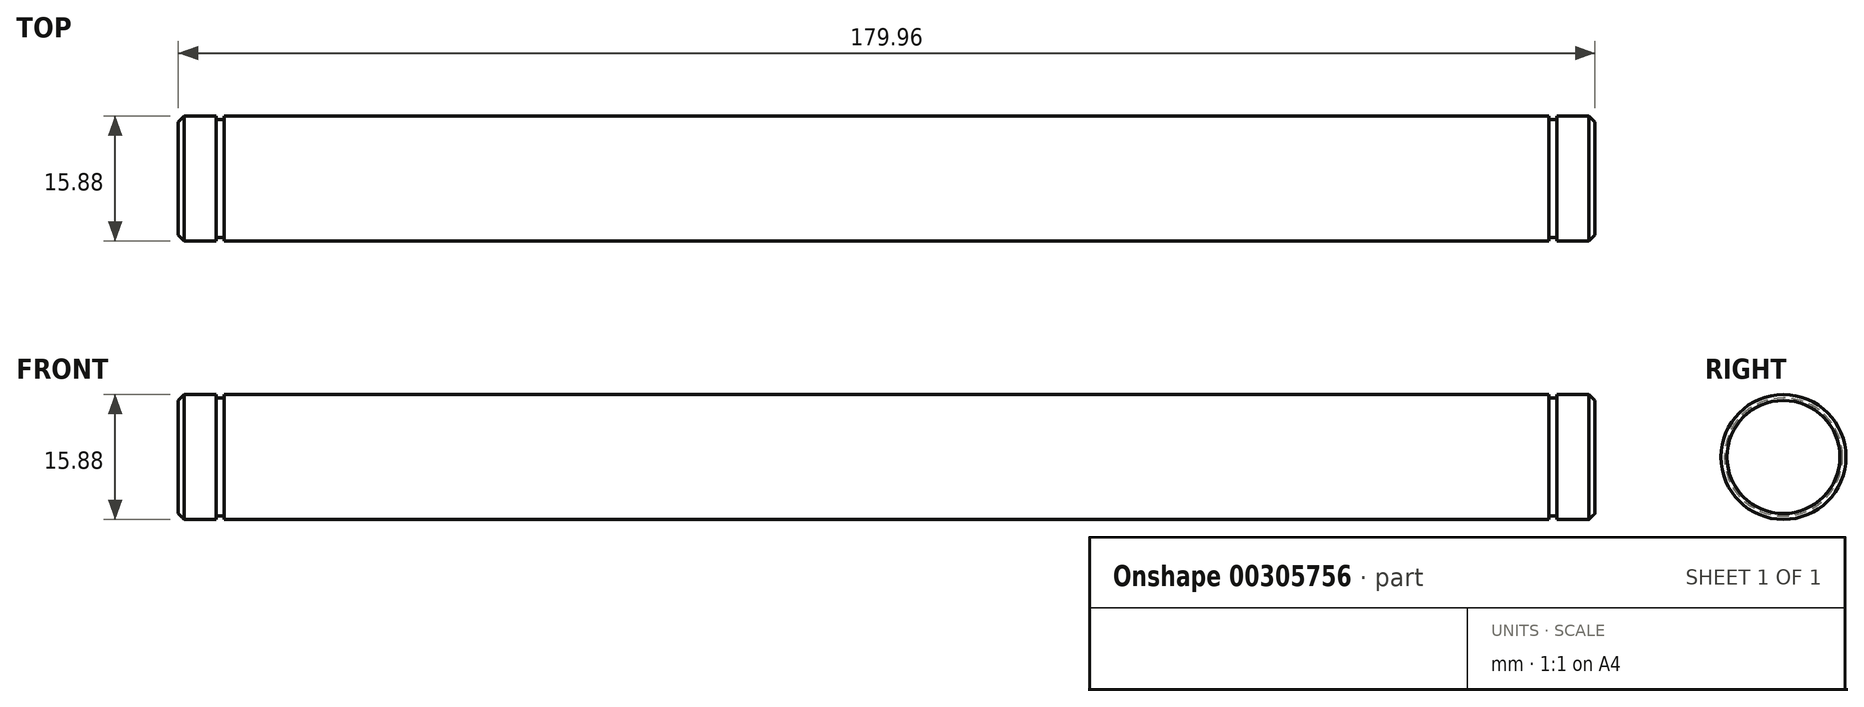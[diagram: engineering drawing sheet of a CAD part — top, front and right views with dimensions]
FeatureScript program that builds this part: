
annotation { "Feature Type Name" : "Feature", "Feature Type Description" : "" }
export const myFeature = defineFeature(function(context is Context, id is Id, definition is map)
    precondition{}
    {
        {
            var Q0;
            Q0=qCreatedBy(makeId("Right.planeOp"),FACE);
            var sketch = newSketch(context, id + "F0", { "sketchPlane" : qUnion([Q0])});
            skCircle(sketch, "E0", {"center": v(0, 0) * mm, "radius": 7.94 * mm});
            skSolve(sketch);
        }
        {
            var Q0;
            Q0 = qSketchRegion(id + "F0", true);
            extrude(context, id + "F1", {"entities" : qUnion([Q0]), "endBound" : BoundingType.SYMMETRIC, "depth" : 168.27 * mm});
        }
        {
            var Q0;
            Q0=makeQuery(id+"F1.opExtrude","CAP_FACE",FACE,{"disambiguationData":[OSD([sQuery(id+"F0.wireOp",EDGE,"E0")])],"isStart":false});
            var sketch = newSketch(context, id + "F2", { "sketchPlane" : qUnion([Q0])});
            skCircle(sketch, "E1", {"center": v(0, 0) * mm, "radius": 7.5 * mm});
            skSolve(sketch);
        }
        {
            var Q0;
            Q0 = qSketchRegion(id + "F2", true);
            extrude(context, id + "F3", {"entities" : qUnion([Q0]), "depth" : 1.02 * mm});
        }
        {
            var Q0;
            Q0=makeQuery(id+"F3.opExtrude","CAP_FACE",FACE,{"disambiguationData":[OSD([sQuery(id+"F2.wireOp",EDGE,"E1")])],"isStart":false});
            var sketch = newSketch(context, id + "F4", { "sketchPlane" : qUnion([Q0])});
            skCircle(sketch, "E2", {"center": v(0, 0) * mm, "radius": 7.94 * mm});
            skSolve(sketch);
        }
        {
            var Q0;
            Q0 = qSketchRegion(id + "F4", true);
            extrude(context, id + "F5", {"entities" : qUnion([Q0]), "operationType" : NewBodyOperationType.ADD, "depth" : 4.83 * mm});
        }
        {
            var Q0;
            Q0=makeQuery(id+"F5.opExtrude","CAP_FACE",FACE,{"disambiguationData":[OSD([sQuery(id+"F4.wireOp",EDGE,"E2")])],"isStart":false});
            chamfer(context, id + "F6", {"entities" : qUnion([Q0]), "width" : 0.76 * mm, "tangentPropagation" : true});
        }
        {
            var Q0;
            Q0=makeQuery(id+"F3.opExtrude","SWEPT_BODY",BODY,{"disambiguationData":[OSD([sQuery(id+"F2.wireOp",EDGE,"E1")])]});
            var Q1;
            Q1=qCreatedBy(makeId("Right.planeOp"),FACE);
            mirror(context, id + "F7", {"operationType" : NewBodyOperationType.ADD, "entities" : qUnion([Q0]), "mirrorPlane" : qUnion([Q1])});
        }
    });
